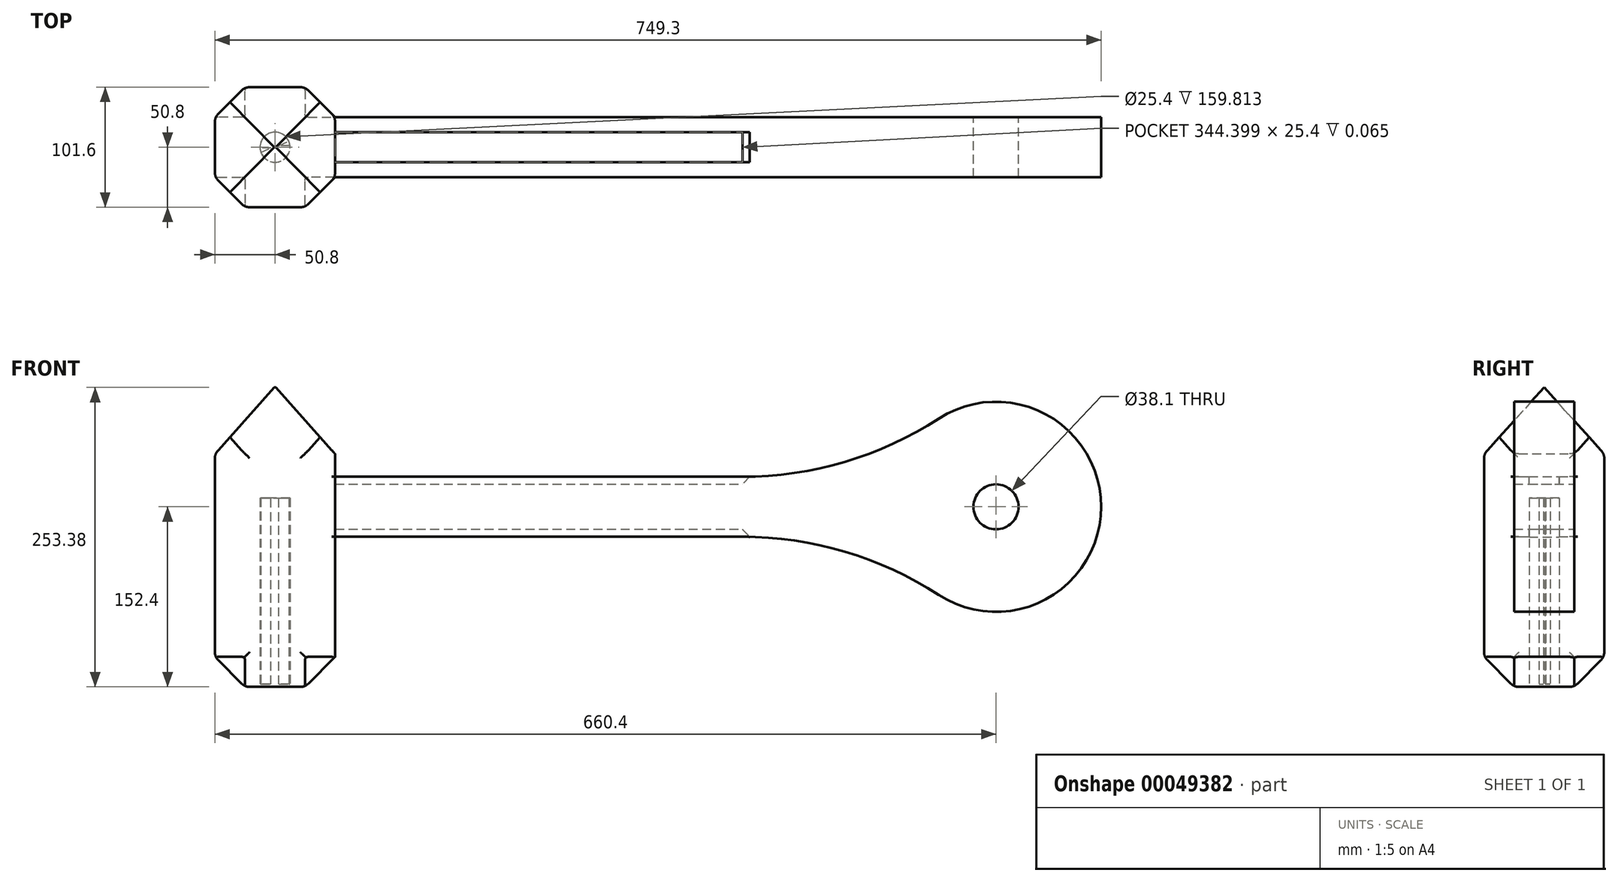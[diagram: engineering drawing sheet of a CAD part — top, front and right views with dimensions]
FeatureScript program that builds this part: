
annotation { "Feature Type Name" : "Feature", "Feature Type Description" : "" }
export const myFeature = defineFeature(function(context is Context, id is Id, definition is map)
    precondition{}
    {
        {
            var Q0;
            Q0=qCreatedBy(makeId("Front.planeOp"),FACE);
            var sketch = newSketch(context, id + "F0", { "sketchPlane" : qUnion([Q0])});
            skCircle(sketch, "E0", {"center": v(0, 0) * mm, "radius": 19.05 * mm});
            skArc(sketch, "E1", {"start": v(-48.41, -74.56) * mm, "mid": v(88.9, 0) * mm, "end": v(-48.41, 74.56) * mm});
            skLineSegment(sketch, "E2.bottom", {"start": v(-214.4, 25.4) * mm, "end": v(-558.8, 25.4) * mm});
            skLineSegment(sketch, "E2.top", {"start": v(-214.4, -25.4) * mm, "end": v(-558.8, -25.4) * mm});
            skLineSegment(sketch, "E2.right", {"start": v(-558.8, 25.4) * mm, "end": v(-558.8, -25.4) * mm});
            skPoint(sketch, "E3.visualSharp", {"position": v(-85.2, -25.4) * mm});
            skArc(sketch, "E3.filletArc", {"start": v(-48.41, -74.56) * mm, "mid": v(-127.84, -37.95) * mm, "end": v(-214.4, -25.4) * mm});
            skPoint(sketch, "E4.visualSharp", {"position": v(-85.2, 25.4) * mm});
            skArc(sketch, "E4.filletArc", {"start": v(-214.4, 25.4) * mm, "mid": v(-127.84, 37.95) * mm, "end": v(-48.41, 74.56) * mm});
            skSolve(sketch);
        }
        {
            var Q0;
            Q0 = qSketchRegion(id + "F0", true);
            extrude(context, id + "F1", {"entities" : qUnion([Q0]), "depth" : 50.8 * mm});
        }
        {
            var Q0;
            Q0=makeQuery(id+"F1.opExtrude","SWEPT_FACE",FACE,{"disambiguationData":[OSD([sQuery(id+"F0.wireOp",EDGE,"E2.right")])]});
            var sketch = newSketch(context, id + "F2", { "sketchPlane" : qUnion([Q0])});
            skLineSegment(sketch, "E5.bottom", {"start": v(-25.4, 101.6) * mm, "end": v(76.2, 101.6) * mm});
            skLineSegment(sketch, "E5.top", {"start": v(-25.4, -152.4) * mm, "end": v(76.2, -152.4) * mm});
            skLineSegment(sketch, "E5.left", {"start": v(-25.4, 101.6) * mm, "end": v(-25.4, -152.4) * mm});
            skLineSegment(sketch, "E5.right", {"start": v(76.2, 101.6) * mm, "end": v(76.2, -152.4) * mm});
            skSolve(sketch);
        }
        {
            var Q0;
            Q0 = qSketchRegion(id + "F2", true);
            extrude(context, id + "F3", {"entities" : qUnion([Q0]), "operationType" : NewBodyOperationType.ADD, "depth" : 101.6 * mm});
        }
        {
            var Q0;
            Q0=makeQuery(id+"F3.opExtrude","SWEPT_FACE",FACE,{"disambiguationData":[OSD([sQuery(id+"F2.wireOp",EDGE,"E5.left")])]});
            var sketch = newSketch(context, id + "F4", { "sketchPlane" : qUnion([Q0])});
            skLineSegment(sketch, "E6", {"start": v(558.8, 44.73) * mm, "end": v(609.6, 101.6) * mm});
            skLineSegment(sketch, "E7", {"start": v(609.6, 101.6) * mm, "end": v(660.4, 44.73) * mm});
            skLineSegment(sketch, "E8", {"start": v(660.4, 44.73) * mm, "end": v(660.4, 124.75) * mm});
            skLineSegment(sketch, "E9", {"start": v(660.4, 124.75) * mm, "end": v(534.59, 124.75) * mm});
            skLineSegment(sketch, "E10", {"start": v(534.59, 124.75) * mm, "end": v(558.8, 44.73) * mm});
            skSolve(sketch);
        }
        {
            var Q0;
            Q0 = qSketchRegion(id + "F4", true);
            extrude(context, id + "F5", {"entities" : qUnion([Q0]), "operationType" : NewBodyOperationType.REMOVE, "oppositeDirection" : true, "depth" : 150 * mm});
        }
        {
            var Q0;
            Q0=makeQuery(id+"F3.opExtrude","CAP_FACE",FACE,{"disambiguationData":[OSD([sQuery(id+"F2.wireOp",EDGE,"E5.bottom"),sQuery(id+"F2.wireOp",EDGE,"E5.top"),sQuery(id+"F2.wireOp",EDGE,"E5.left"),sQuery(id+"F2.wireOp",EDGE,"E5.right")])],"isStart":false});
            var sketch = newSketch(context, id + "F6", { "sketchPlane" : qUnion([Q0])});
            skLineSegment(sketch, "E11", {"start": v(-25.4, 44.73) * mm, "end": v(25.4, 100.98) * mm});
            skLineSegment(sketch, "E12", {"start": v(25.4, 100.98) * mm, "end": v(76.2, 44.73) * mm});
            skLineSegment(sketch, "E13", {"start": v(76.2, 44.73) * mm, "end": v(85.72, 107.49) * mm});
            skLineSegment(sketch, "E14", {"start": v(85.72, 107.49) * mm, "end": v(-36, 107.49) * mm});
            skLineSegment(sketch, "E15", {"start": v(-36, 107.49) * mm, "end": v(-25.4, 44.73) * mm});
            skSolve(sketch);
        }
        {
            var Q0;
            Q0 = qSketchRegion(id + "F6", true);
            extrude(context, id + "F7", {"entities" : qUnion([Q0]), "operationType" : NewBodyOperationType.REMOVE, "oppositeDirection" : true, "depth" : 133.97 * mm});
        }
        {
            var Q0;
            Q0=makeQuery(id+"F3.opExtrude","CAP_EDGE",EDGE,{"disambiguationData":[OSD([sQuery(id+"F2.wireOp",EDGE,"E5.right")])],"isStart":false});
            var Q1;
            Q1=makeQuery(id+"F3.opExtrude","CAP_EDGE",EDGE,{"disambiguationData":[OSD([sQuery(id+"F2.wireOp",EDGE,"E5.right")])],"isStart":true});
            var Q2;
            Q2=makeQuery(id+"F3.opExtrude","CAP_EDGE",EDGE,{"disambiguationData":[OSD([sQuery(id+"F2.wireOp",EDGE,"E5.left")])],"isStart":true});
            var Q3;
            Q3=makeQuery(id+"F3.opExtrude","CAP_EDGE",EDGE,{"disambiguationData":[OSD([sQuery(id+"F2.wireOp",EDGE,"E5.left")])],"isStart":false});
            var Q4;
            Q4=makeQuery(id+"F3.opExtrude","SWEPT_FACE",FACE,{"disambiguationData":[OSD([sQuery(id+"F2.wireOp",EDGE,"E5.top")])]});
            chamfer(context, id + "F8", {"entities" : qUnion([Q0, Q1, Q2, Q3, Q4]), "width" : 25.4 * mm, "tangentPropagation" : true});
        }
        {
            var Q0;
            Q0=makeQuery(id+"F3.opExtrude","SWEPT_FACE",FACE,{"disambiguationData":[OSD([sQuery(id+"F2.wireOp",EDGE,"E5.top")])]});
            fillet(context, id + "F9", {"entities" : qUnion([Q0]), "radius" : 9.52 * mm, "tangentPropagation" : true, "allowEdgeOverflow" : false});
        }
        {
            var Q0;
            Q0=makeQuery(id+"F3.opExtrude","SWEPT_FACE",FACE,{"disambiguationData":[OSD([sQuery(id+"F2.wireOp",EDGE,"E5.right")])]});
            var Q1;
            Q1=makeQuery(id+"F3.opExtrude","SWEPT_FACE",FACE,{"disambiguationData":[OSD([sQuery(id+"F2.wireOp",EDGE,"E5.left")])]});
            var Q2;
            Q2=makeQuery(id+"F3.opExtrude","CAP_FACE",FACE,{"disambiguationData":[OSD([sQuery(id+"F2.wireOp",EDGE,"E5.bottom"),sQuery(id+"F2.wireOp",EDGE,"E5.top"),sQuery(id+"F2.wireOp",EDGE,"E5.left"),sQuery(id+"F2.wireOp",EDGE,"E5.right")])],"isStart":false});
            fillet(context, id + "F10", {"entities" : qUnion([Q0, Q1, Q2]), "radius" : 9.52 * mm, "tangentPropagation" : true, "allowEdgeOverflow" : false});
        }
        {
            var Q0;
            {var subQ0=sQuery(id+"F2.wireOp",EDGE,"E5.right");Q0=makeQuery(id+"F8.opChamfer","BLEND_EDGE",EDGE,{"disambiguationData":[OD(1.0)],"blendedFrom":[makeQuery(id+"F3.opExtrude","CAP_EDGE",EDGE,{"disambiguationData":[OSD([subQ0])],"isStart":true}),makeQuery(id+"F3.opExtrude","CAP_FACE",FACE,{"disambiguationData":[OSD([sQuery(id+"F2.wireOp",EDGE,"E5.bottom"),sQuery(id+"F2.wireOp",EDGE,"E5.top"),sQuery(id+"F2.wireOp",EDGE,"E5.left"),subQ0])],"isStart":true})],"blendedInto":[makeQuery(id+"F3.opExtrude","CAP_FACE",FACE,{"disambiguationData":[OSD([sQuery(id+"F2.wireOp",EDGE,"E5.bottom"),sQuery(id+"F2.wireOp",EDGE,"E5.top"),sQuery(id+"F2.wireOp",EDGE,"E5.left"),subQ0])],"isStart":true})]});}
            var Q1;
            {var subQ0=sQuery(id+"F2.wireOp",EDGE,"E5.left");Q1=makeQuery(id+"F8.opChamfer","BLEND_EDGE",EDGE,{"disambiguationData":[OD(1.0)],"blendedFrom":[makeQuery(id+"F3.opExtrude","CAP_EDGE",EDGE,{"disambiguationData":[OSD([subQ0])],"isStart":true}),makeQuery(id+"F3.opExtrude","CAP_FACE",FACE,{"disambiguationData":[OSD([sQuery(id+"F2.wireOp",EDGE,"E5.bottom"),sQuery(id+"F2.wireOp",EDGE,"E5.top"),subQ0,sQuery(id+"F2.wireOp",EDGE,"E5.right")])],"isStart":true})],"blendedInto":[makeQuery(id+"F3.opExtrude","CAP_FACE",FACE,{"disambiguationData":[OSD([sQuery(id+"F2.wireOp",EDGE,"E5.bottom"),sQuery(id+"F2.wireOp",EDGE,"E5.top"),subQ0,sQuery(id+"F2.wireOp",EDGE,"E5.right")])],"isStart":true})]});}
            fillet(context, id + "F11", {"entities" : qUnion([Q0, Q1]), "radius" : 9.52 * mm, "tangentPropagation" : true, "allowEdgeOverflow" : false});
        }
        {
            var Q0;
            {var subQ0=sQuery(id+"F2.wireOp",EDGE,"E5.right");Q0=makeQuery(id+"F8.opChamfer","BLEND_EDGE",EDGE,{"disambiguationData":[OD(0.0)],"blendedFrom":[makeQuery(id+"F3.opExtrude","CAP_EDGE",EDGE,{"disambiguationData":[OSD([subQ0])],"isStart":true}),makeQuery(id+"F3.opExtrude","CAP_FACE",FACE,{"disambiguationData":[OSD([sQuery(id+"F2.wireOp",EDGE,"E5.bottom"),sQuery(id+"F2.wireOp",EDGE,"E5.top"),sQuery(id+"F2.wireOp",EDGE,"E5.left"),subQ0])],"isStart":true})],"blendedInto":[makeQuery(id+"F3.opExtrude","CAP_FACE",FACE,{"disambiguationData":[OSD([sQuery(id+"F2.wireOp",EDGE,"E5.bottom"),sQuery(id+"F2.wireOp",EDGE,"E5.top"),sQuery(id+"F2.wireOp",EDGE,"E5.left"),subQ0])],"isStart":true})]});}
            var Q1;
            {var subQ0=sQuery(id+"F2.wireOp",EDGE,"E5.left");Q1=makeQuery(id+"F8.opChamfer","BLEND_EDGE",EDGE,{"disambiguationData":[OD(0.0)],"blendedFrom":[makeQuery(id+"F3.opExtrude","CAP_EDGE",EDGE,{"disambiguationData":[OSD([subQ0])],"isStart":true}),makeQuery(id+"F3.opExtrude","CAP_FACE",FACE,{"disambiguationData":[OSD([sQuery(id+"F2.wireOp",EDGE,"E5.bottom"),sQuery(id+"F2.wireOp",EDGE,"E5.top"),subQ0,sQuery(id+"F2.wireOp",EDGE,"E5.right")])],"isStart":true})],"blendedInto":[makeQuery(id+"F3.opExtrude","CAP_FACE",FACE,{"disambiguationData":[OSD([sQuery(id+"F2.wireOp",EDGE,"E5.bottom"),sQuery(id+"F2.wireOp",EDGE,"E5.top"),subQ0,sQuery(id+"F2.wireOp",EDGE,"E5.right")])],"isStart":true})]});}
            fillet(context, id + "F12", {"entities" : qUnion([Q0, Q1]), "radius" : 9.52 * mm, "tangentPropagation" : true, "allowEdgeOverflow" : false});
        }
        {
            var Q0;
            Q0=makeQuery(id+"F3.opExtrude","SWEPT_FACE",FACE,{"disambiguationData":[OSD([sQuery(id+"F2.wireOp",EDGE,"E5.top")])]});
            var sketch = newSketch(context, id + "F13", { "sketchPlane" : qUnion([Q0])});
            skCircle(sketch, "E16", {"center": v(-609.6, 25.4) * mm, "radius": 12.7 * mm});
            skLineSegment(sketch, "E17", {"start": v(-631.05, 46.85) * mm, "end": v(-588.15, 3.95) * mm, "construction": true});
            skLineSegment(sketch, "E18", {"start": v(-588.15, 3.95) * mm, "end": v(-588.15, 46.85) * mm, "construction": true});
            skLineSegment(sketch, "E19", {"start": v(-588.15, 46.85) * mm, "end": v(-631.05, 3.95) * mm, "construction": true});
            skSolve(sketch);
        }
        {
            var Q0;
            Q0 = qSketchRegion(id + "F13", true);
            extrude(context, id + "F14", {"entities" : qUnion([Q0]), "operationType" : NewBodyOperationType.REMOVE, "oppositeDirection" : true, "depth" : 159.8 * mm});
        }
        {
            var Q0;
            Q0=makeQuery(id+"F1.opExtrude","SWEPT_FACE",FACE,{"disambiguationData":[OSD([sQuery(id+"F0.wireOp",EDGE,"E2.bottom")])]});
            var sketch = newSketch(context, id + "F15", { "sketchPlane" : qUnion([Q0])});
            skLineSegment(sketch, "E20.bottom", {"start": v(-558.8, -12.7) * mm, "end": v(-214.4, -12.7) * mm});
            skLineSegment(sketch, "E20.top", {"start": v(-558.8, -38.1) * mm, "end": v(-214.4, -38.1) * mm});
            skLineSegment(sketch, "E20.left", {"start": v(-558.8, -12.7) * mm, "end": v(-558.8, -38.1) * mm});
            skLineSegment(sketch, "E20.right", {"start": v(-214.4, -12.7) * mm, "end": v(-214.4, -38.1) * mm});
            skSolve(sketch);
        }
        {
            var Q0;
            Q0 = qSketchRegion(id + "F15", true);
            extrude(context, id + "F16", {"entities" : qUnion([Q0]), "operationType" : NewBodyOperationType.REMOVE, "oppositeDirection" : true, "depth" : 6.35 * mm});
        }
        {
            var Q0;
            Q0=makeQuery(id+"F1.opExtrude","SWEPT_FACE",FACE,{"disambiguationData":[OSD([sQuery(id+"F0.wireOp",EDGE,"E2.top")])]});
            var sketch = newSketch(context, id + "F17", { "sketchPlane" : qUnion([Q0])});
            skLineSegment(sketch, "E21.bottom", {"start": v(-558.8, 12.7) * mm, "end": v(-214.4, 12.7) * mm});
            skLineSegment(sketch, "E21.top", {"start": v(-558.8, 38.1) * mm, "end": v(-214.4, 38.1) * mm});
            skLineSegment(sketch, "E21.left", {"start": v(-558.8, 12.7) * mm, "end": v(-558.8, 38.1) * mm});
            skLineSegment(sketch, "E21.right", {"start": v(-214.4, 12.7) * mm, "end": v(-214.4, 38.1) * mm});
            skSolve(sketch);
        }
        {
            var Q0;
            Q0 = qSketchRegion(id + "F17", true);
            extrude(context, id + "F18", {"entities" : qUnion([Q0]), "operationType" : NewBodyOperationType.REMOVE, "oppositeDirection" : true, "depth" : 6.35 * mm});
        }
        {
            var Q0;
            Q0=makeQuery(id+"F18.boolean.opBoolean","MERGE",EDGE,{"derivedFrom":[makeQuery(id+"F1.opExtrude","SWEPT_EDGE",EDGE,{"disambiguationData":[OSD([sQuery(id+"F0.wireOp",EDGE,"E2.top"),sQuery(id+"F0.wireOp",EDGE,"E3.filletArc")])]}),makeQuery(id+"F18.opExtrude","CAP_EDGE",EDGE,{"disambiguationData":[OSD([sQuery(id+"F17.wireOp",EDGE,"E21.right")])],"isStart":true})]});
            var Q1;
            Q1=makeQuery(id+"F16.boolean.opBoolean","MERGE",EDGE,{"derivedFrom":[makeQuery(id+"F1.opExtrude","SWEPT_EDGE",EDGE,{"disambiguationData":[OSD([sQuery(id+"F0.wireOp",EDGE,"E2.bottom"),sQuery(id+"F0.wireOp",EDGE,"E4.filletArc")])]}),makeQuery(id+"F16.opExtrude","CAP_EDGE",EDGE,{"disambiguationData":[OSD([sQuery(id+"F15.wireOp",EDGE,"E20.right")])],"isStart":true})]});
            chamfer(context, id + "F19", {"entities" : qUnion([Q0, Q1]), "width" : 6.35 * mm, "tangentPropagation" : true});
        }
        {
            var Q0;
            Q0=makeQuery(id+"F14.boolean.opBoolean","COPY",FACE,{"derivedFrom":makeQuery(id+"F14.opExtrude","CAP_FACE",FACE,{"disambiguationData":[OSD([sQuery(id+"F13.wireOp",EDGE,"E16")])],"isStart":false})});
            var sketch = newSketch(context, id + "F20", { "sketchPlane" : qUnion([Q0])});
            skLineSegment(sketch, "E22", {"start": v(-626.38, 31.78) * mm, "end": v(-613.03, 25.98) * mm});
            skLineSegment(sketch, "E23", {"start": v(-613.03, 25.98) * mm, "end": v(-628.4, 25.98) * mm});
            skLineSegment(sketch, "E24", {"start": v(-628.4, 25.98) * mm, "end": v(-626.38, 31.78) * mm});
            skLineSegment(sketch, "E25", {"start": v(-606.24, 24.22) * mm, "end": v(-591.88, 17.42) * mm});
            skLineSegment(sketch, "E26", {"start": v(-591.88, 17.42) * mm, "end": v(-591.88, 23.97) * mm});
            skLineSegment(sketch, "E27", {"start": v(-591.88, 23.97) * mm, "end": v(-606.24, 24.22) * mm});
            skSolve(sketch);
        }
        {
            var Q0;
            Q0 = qSketchRegion(id + "F20", true);
            extrude(context, id + "F21", {"entities" : qUnion([Q0]), "operationType" : NewBodyOperationType.ADD, "depth" : 157.55 * mm});
        }
    });
